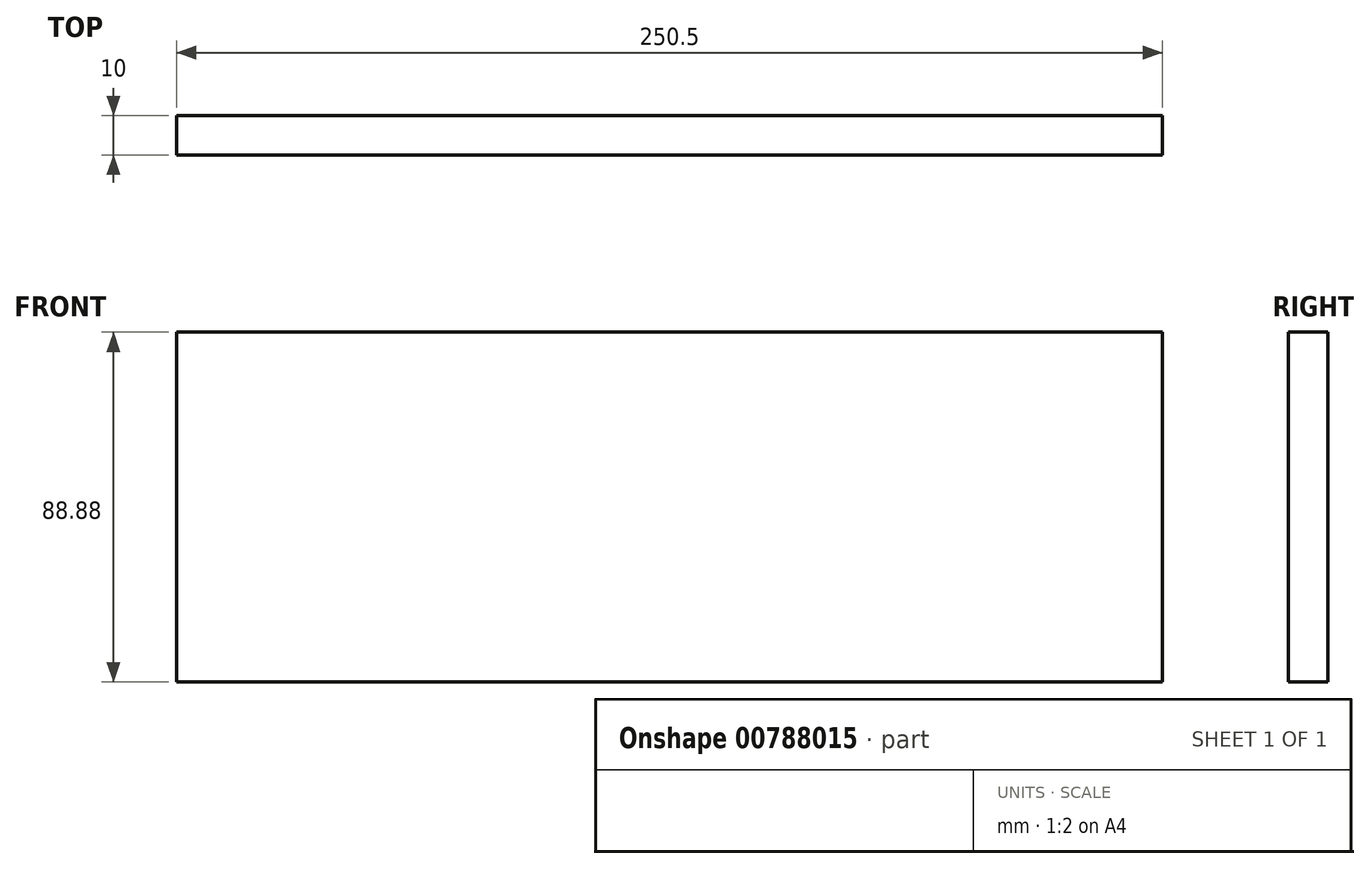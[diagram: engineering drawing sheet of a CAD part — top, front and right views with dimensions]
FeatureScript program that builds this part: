
annotation { "Feature Type Name" : "Feature", "Feature Type Description" : "" }
export const myFeature = defineFeature(function(context is Context, id is Id, definition is map)
    precondition{}
    {
        {
            var Q0;
            Q0=qCreatedBy(makeId("Front.planeOp"),FACE);
            var sketch = newSketch(context, id + "F0", { "sketchPlane" : qUnion([Q0])});
            skLineSegment(sketch, "E0.bottom", {"start": v(125.25, 44.44) * mm, "end": v(-125.25, 44.44) * mm});
            skLineSegment(sketch, "E0.top", {"start": v(125.25, -44.44) * mm, "end": v(-125.25, -44.44) * mm});
            skLineSegment(sketch, "E0.left", {"start": v(125.25, 44.44) * mm, "end": v(125.25, -44.44) * mm});
            skLineSegment(sketch, "E0.right", {"start": v(-125.25, 44.44) * mm, "end": v(-125.25, -44.44) * mm});
            skPoint(sketch, "E0.middle", {"position": v(0, 0) * mm});
            skSolve(sketch);
        }
        {
            var Q0;
            Q0 = qSketchRegion(id + "F0", true);
            extrude(context, id + "F1", {"entities" : qUnion([Q0]), "depth" : 10 * mm, "offsetDistance" : 25.4 * mm});
        }
    });
